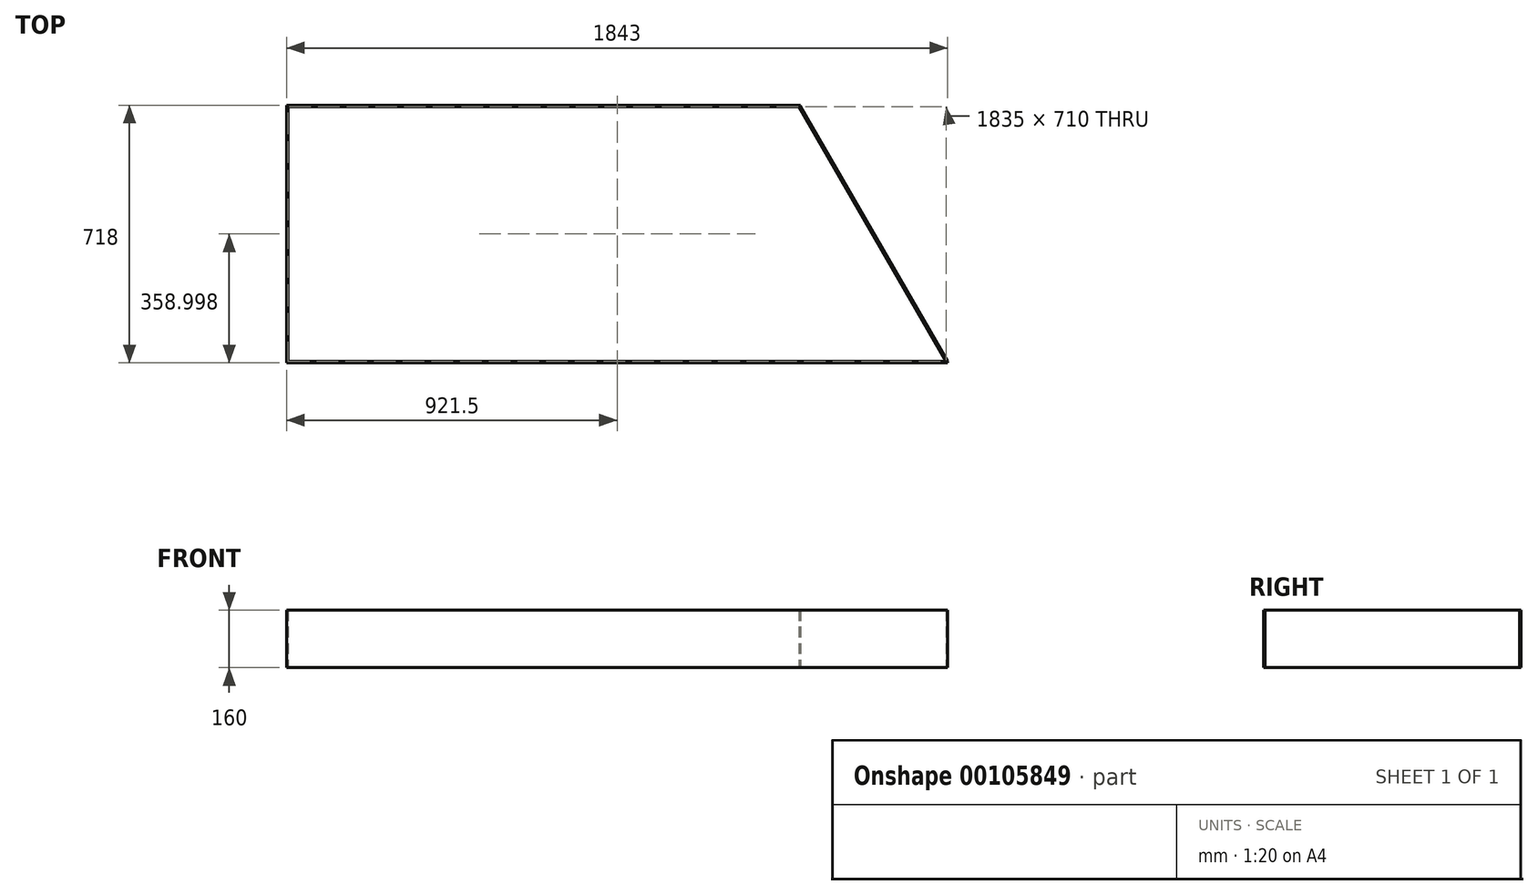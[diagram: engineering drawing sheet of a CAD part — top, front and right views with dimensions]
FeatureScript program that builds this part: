
annotation { "Feature Type Name" : "Feature", "Feature Type Description" : "" }
export const myFeature = defineFeature(function(context is Context, id is Id, definition is map)
    precondition{}
    {
        {
            var Q0;
            Q0=qCreatedBy(makeId("Top.planeOp"),FACE);
            var sketch = newSketch(context, id + "F0", { "sketchPlane" : qUnion([Q0])});
            skLineSegment(sketch, "E0", {"start": v(0, 20.82) * mm, "end": v(0, 730.82) * mm});
            skLineSegment(sketch, "E1", {"start": v(0, 730.82) * mm, "end": v(1425, 730.82) * mm});
            skLineSegment(sketch, "E2", {"start": v(1425, 730.82) * mm, "end": v(1835, 20.82) * mm});
            skLineSegment(sketch, "E3", {"start": v(0, 20.82) * mm, "end": v(1835, 20.82) * mm});
            skLineSegment(sketch, "E4", {"start": v(0, 16.82) * mm, "end": v(1835, 16.82) * mm});
            skLineSegment(sketch, "E5", {"start": v(1839, 20.82) * mm, "end": v(1429, 730.82) * mm});
            skLineSegment(sketch, "E6", {"start": v(1425, 734.82) * mm, "end": v(0, 734.82) * mm});
            skLineSegment(sketch, "E7", {"start": v(-4, 730.82) * mm, "end": v(-4, 20.82) * mm});
            skLineSegment(sketch, "E8", {"start": v(-4, 20.82) * mm, "end": v(-4, 16.82) * mm});
            skLineSegment(sketch, "E9", {"start": v(-4, 16.82) * mm, "end": v(0, 16.82) * mm});
            skLineSegment(sketch, "E10", {"start": v(-4, 730.82) * mm, "end": v(-4, 734.82) * mm});
            skLineSegment(sketch, "E11", {"start": v(-4, 734.82) * mm, "end": v(0, 734.82) * mm});
            skLineSegment(sketch, "E12", {"start": v(1835, 16.82) * mm, "end": v(1839, 16.82) * mm});
            skLineSegment(sketch, "E13", {"start": v(1839, 16.82) * mm, "end": v(1839, 20.82) * mm});
            skPoint(sketch, "E14.start.orphan", {"position": v(1426.7, 734.82) * mm});
            skLineSegment(sketch, "E15", {"start": v(1426.7, 734.82) * mm, "end": v(1425, 734.82) * mm});
            skPoint(sketch, "E16.end.orphan", {"position": v(1429, 734.82) * mm});
            skLineSegment(sketch, "E17", {"start": v(1426.7, 734.82) * mm, "end": v(1429, 734.82) * mm});
            skLineSegment(sketch, "E18", {"start": v(1429, 730.82) * mm, "end": v(1429, 734.82) * mm});
            skSolve(sketch);
        }
        {
            var Q0;
            Q0 = qSketchRegion(id + "F0", true);
            extrude(context, id + "F1", {"entities" : qUnion([Q0]), "depth" : 160 * mm});
        }
    });
